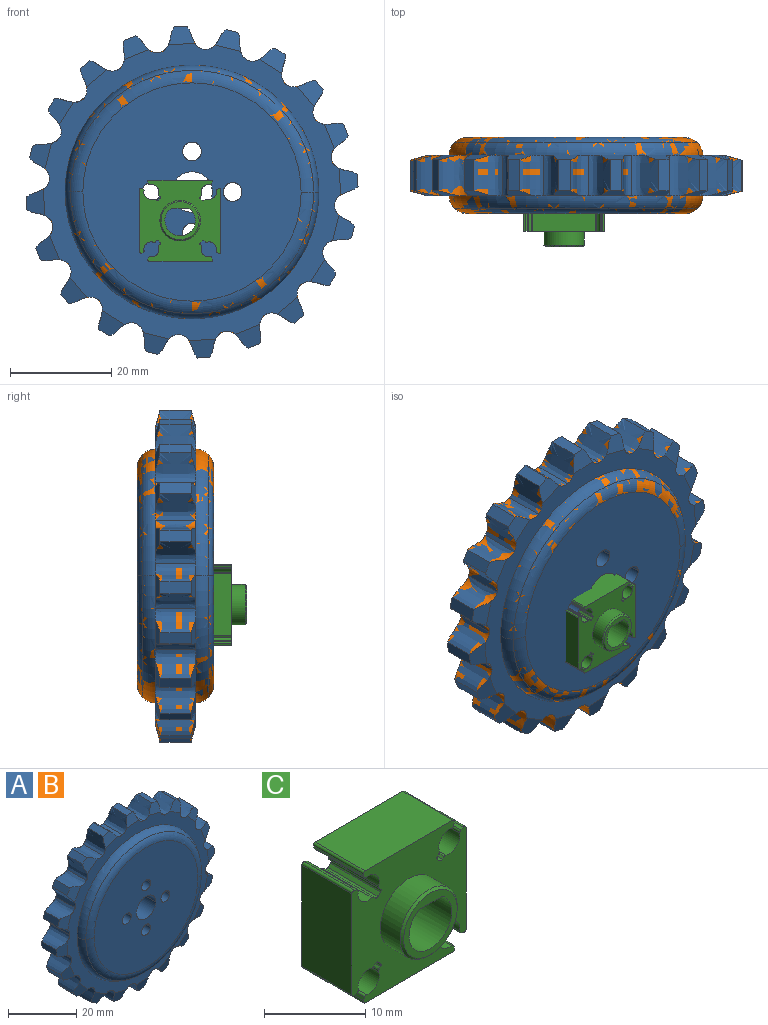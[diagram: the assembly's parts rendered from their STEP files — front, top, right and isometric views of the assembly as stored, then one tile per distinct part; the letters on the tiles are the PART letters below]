
ASSEMBLY  parts=3 mates=1
PART A: 134 faces, bbox 65.6x15.1x65.6 mm
  f0: plane 5.09x4.35mm, normal (-0.06,0.97,-0.25), area 14.3mm2, adj f1,f40,f43,f45
  f1: plane 6.12x2.3mm, normal (-0.24,0,-0.97), area 14.5mm2, adj f0,f43,f44,f45
  f2: plane 5.24x3.8mm, normal (0.02,0.97,-0.26), area 14.3mm2, adj f3,f40,f46,f48
  f3: plane 6.12x2.37mm, normal (0.07,0,-1), area 14.5mm2, adj f2,f46,f47,f48
  f4: plane 5.06x4.71mm, normal (0.1,0.97,-0.24), area 14.3mm2, adj f5,f40,f49,f51
  f5: plane 6.12x2.2mm, normal (0.37,0,-0.93), area 14.5mm2, adj f4,f49,f50,f51
  f6: plane 5.2x5.16mm, normal (0.17,0.97,-0.2), area 14.3mm2, adj f7,f40,f52,f54
  f7: plane 6.12x1.82mm, normal (0.64,0,-0.77), area 14.5mm2, adj f6,f52,f53,f54
  f8: plane 5.15x5.02mm, normal (0.22,0.97,-0.14), area 14.3mm2, adj f9,f40,f55,f57
  f9: plane 6.12x2.01mm, normal (0.85,0,-0.53), area 14.5mm2, adj f8,f55,f56,f57
  f10: plane 5.09x4.35mm, normal (0.25,0.97,-0.06), area 14.3mm2, adj f11,f40,f58,f60
  f11: plane 6.12x2.3mm, normal (0.97,0,-0.24), area 14.5mm2, adj f10,f58,f59,f60
  f12: plane 5.24x3.8mm, normal (0.26,0.97,0.02), area 14.3mm2, adj f13,f40,f61,f63
  f13: plane 6.12x2.37mm, normal (1,0,0.07), area 14.5mm2, adj f12,f61,f62,f63
  f14: plane 5.06x4.71mm, normal (0.24,0.97,0.1), area 14.3mm2, adj f15,f40,f64,f66
  f15: plane 6.12x2.2mm, normal (0.93,0,0.37), area 14.5mm2, adj f14,f64,f65,f66
  f16: plane 5.2x5.16mm, normal (0.2,0.97,0.17), area 14.3mm2, adj f17,f40,f67,f69
  f17: plane 6.12x1.82mm, normal (0.77,0,0.64), area 14.5mm2, adj f16,f67,f68,f69
  f18: plane 5.15x5.02mm, normal (0.14,0.97,0.22), area 14.3mm2, adj f19,f40,f70,f72
  f19: plane 6.12x2.01mm, normal (0.53,0,0.85), area 14.5mm2, adj f18,f70,f71,f72
  f20: plane 5.09x4.35mm, normal (0.06,0.97,0.25), area 14.3mm2, adj f21,f40,f73,f75
  f21: plane 6.12x2.3mm, normal (0.24,0,0.97), area 14.5mm2, adj f20,f73,f74,f75
  f22: plane 5.24x3.8mm, normal (-0.02,0.97,0.26), area 14.3mm2, adj f23,f40,f76,f78
  f23: plane 6.12x2.37mm, normal (-0.07,0,1), area 14.5mm2, adj f22,f76,f77,f78
  f24: plane 5.06x4.71mm, normal (-0.1,0.97,0.24), area 14.3mm2, adj f25,f40,f79,f81
  f25: plane 6.12x2.2mm, normal (-0.37,0,0.93), area 14.5mm2, adj f24,f79,f80,f81
  f26: plane 5.2x5.16mm, normal (-0.17,0.97,0.2), area 14.3mm2, adj f27,f40,f82,f84
  f27: plane 6.12x1.82mm, normal (-0.64,0,0.77), area 14.5mm2, adj f26,f82,f83,f84
  f28: plane 5.15x5.02mm, normal (-0.22,0.97,0.14), area 14.3mm2, adj f29,f40,f85,f87
  f29: plane 6.12x2.01mm, normal (-0.85,0,0.53), area 14.5mm2, adj f28,f85,f86,f87
  f30: plane 5.09x4.35mm, normal (-0.25,0.97,0.06), area 14.3mm2, adj f31,f40,f88,f90
  f31: plane 6.12x2.3mm, normal (-0.97,0,0.24), area 14.5mm2, adj f30,f88,f89,f90
  f32: plane 5.24x3.8mm, normal (-0.26,0.97,-0.02), area 14.3mm2, adj f33,f40,f91,f93
  f33: plane 6.12x2.37mm, normal (-1,0,-0.07), area 14.5mm2, adj f32,f91,f92,f93
  f34: plane 5.06x4.71mm, normal (-0.24,0.97,-0.1), area 14.3mm2, adj f35,f40,f94,f96
  f35: plane 6.12x2.2mm, normal (-0.93,0,-0.37), area 14.5mm2, adj f34,f94,f95,f96
  f36: plane 5.2x5.16mm, normal (-0.2,0.97,-0.17), area 14.3mm2, adj f37,f40,f97,f99
  f37: plane 6.12x1.82mm, normal (-0.77,0,-0.64), area 14.5mm2, adj f36,f97,f98,f99
  f38: plane 6.12x2.01mm, normal (-0.53,0,-0.85), area 14.5mm2, adj f39,f41,f42,f100
  f39: plane 5.15x5.02mm, normal (-0.14,0.97,-0.22), area 14.3mm2, adj f38,f40,f42,f100
  f40: plane 58.78x58.78mm, normal (0,1,0), area 667.1mm2, adj f0,f2,f4,f6,f8,f10,f12,f14
  f41: plane 5.15x5.02mm, normal (-0.14,-0.97,-0.22), area 14.3mm2, adj f38,f42,f100,f103
  f42: extruded ~8x5.32mm, area 45.7mm2, adj f38,f39,f40,f41,f43,f103
  f43: extruded ~8x5.51mm, area 45.8mm2, adj f0,f1,f40,f42,f44,f103
  f44: plane 5.09x4.35mm, normal (-0.06,-0.97,-0.25), area 14.3mm2, adj f1,f43,f45,f103
  f45: extruded ~8x4.31mm, area 45.7mm2, adj f0,f1,f40,f44,f46,f103
  f46: extruded ~8x4.64mm, area 45.8mm2, adj f2,f3,f40,f45,f47,f103
  f47: plane 5.24x3.8mm, normal (0.02,-0.97,-0.26), area 14.3mm2, adj f3,f46,f48,f103
  f48: extruded ~8x5.09mm, area 45.7mm2, adj f2,f3,f40,f47,f49,f103
  f49: extruded ~8x4.82mm, area 45.8mm2, adj f4,f5,f40,f48,f50,f103
  f50: plane 5.06x4.71mm, normal (0.1,-0.97,-0.24), area 14.3mm2, adj f5,f49,f51,f103
  f51: extruded ~8x5.73mm, area 45.7mm2, adj f4,f5,f40,f50,f52,f103
  f52: extruded ~8x5.6mm, area 45.8mm2, adj f6,f7,f40,f51,f53,f103
  f53: plane 5.2x5.16mm, normal (0.17,-0.97,-0.2), area 14.3mm2, adj f7,f52,f54,f103
  f54: extruded ~8x5.81mm, area 45.7mm2, adj f6,f7,f40,f53,f55,f103
  f55: extruded ~8x5.84mm, area 45.8mm2, adj f8,f9,f40,f54,f56,f103
  f56: plane 5.15x5.02mm, normal (0.22,-0.97,-0.14), area 14.3mm2, adj f9,f55,f57,f103
  f57: extruded ~8x5.32mm, area 45.7mm2, adj f8,f9,f40,f56,f58,f103
  f58: extruded ~8x5.51mm, area 45.8mm2, adj f10,f11,f40,f57,f59,f103
  f59: plane 5.09x4.35mm, normal (0.25,-0.97,-0.06), area 14.3mm2, adj f11,f58,f60,f103
  f60: extruded ~8x4.31mm, area 45.7mm2, adj f10,f11,f40,f59,f61,f103
  f61: extruded ~8x4.64mm, area 45.8mm2, adj f12,f13,f40,f60,f62,f103
  f62: plane 5.24x3.8mm, normal (0.26,-0.97,0.02), area 14.3mm2, adj f13,f61,f63,f103
  f63: extruded ~8x5.09mm, area 45.7mm2, adj f12,f13,f40,f62,f64,f103
  f64: extruded ~8x4.82mm, area 45.8mm2, adj f14,f15,f40,f63,f65,f103
  f65: plane 5.06x4.71mm, normal (0.24,-0.97,0.1), area 14.3mm2, adj f15,f64,f66,f103
  f66: extruded ~8x5.73mm, area 45.7mm2, adj f14,f15,f40,f65,f67,f103
  f67: extruded ~8x5.6mm, area 45.8mm2, adj f16,f17,f40,f66,f68,f103
  f68: plane 5.2x5.16mm, normal (0.2,-0.97,0.17), area 14.3mm2, adj f17,f67,f69,f103
  f69: extruded ~8x5.81mm, area 45.7mm2, adj f16,f17,f40,f68,f70,f103
  f70: extruded ~8x5.84mm, area 45.8mm2, adj f18,f19,f40,f69,f71,f103
  f71: plane 5.15x5.02mm, normal (0.14,-0.97,0.22), area 14.3mm2, adj f19,f70,f72,f103
  f72: extruded ~8x5.32mm, area 45.7mm2, adj f18,f19,f40,f71,f73,f103
  f73: extruded ~8x5.51mm, area 45.8mm2, adj f20,f21,f40,f72,f74,f103
  f74: plane 5.09x4.35mm, normal (0.06,-0.97,0.25), area 14.3mm2, adj f21,f73,f75,f103
  f75: extruded ~8x4.31mm, area 45.7mm2, adj f20,f21,f40,f74,f76,f103
  f76: extruded ~8x4.64mm, area 45.8mm2, adj f22,f23,f40,f75,f77,f103
  f77: plane 5.24x3.8mm, normal (-0.02,-0.97,0.26), area 14.3mm2, adj f23,f76,f78,f103
  f78: extruded ~8x5.09mm, area 45.7mm2, adj f22,f23,f40,f77,f79,f103
  f79: extruded ~8x4.82mm, area 45.8mm2, adj f24,f25,f40,f78,f80,f103
  f80: plane 5.06x4.71mm, normal (-0.1,-0.97,0.24), area 14.3mm2, adj f25,f79,f81,f103
  f81: extruded ~8x5.73mm, area 45.7mm2, adj f24,f25,f40,f80,f82,f103
  f82: extruded ~8x5.6mm, area 45.8mm2, adj f26,f27,f40,f81,f83,f103
  f83: plane 5.2x5.16mm, normal (-0.17,-0.97,0.2), area 14.3mm2, adj f27,f82,f84,f103
  f84: extruded ~8x5.81mm, area 45.8mm2, adj f26,f27,f40,f83,f85,f103
  f85: extruded ~8x5.84mm, area 45.7mm2, adj f28,f29,f40,f84,f86,f103
  f86: plane 5.15x5.02mm, normal (-0.22,-0.97,0.14), area 14.3mm2, adj f29,f85,f87,f103
  f87: extruded ~8x5.32mm, area 45.7mm2, adj f28,f29,f40,f86,f88,f103
  f88: extruded ~8x5.51mm, area 45.8mm2, adj f30,f31,f40,f87,f89,f103
  f89: plane 5.09x4.35mm, normal (-0.25,-0.97,0.06), area 14.3mm2, adj f31,f88,f90,f103
  f90: extruded ~8x4.31mm, area 45.7mm2, adj f30,f31,f40,f89,f91,f103
  f91: extruded ~8x4.64mm, area 45.8mm2, adj f32,f33,f40,f90,f92,f103
  f92: plane 5.24x3.8mm, normal (-0.26,-0.97,-0.02), area 14.3mm2, adj f33,f91,f93,f103
  f93: extruded ~8x5.09mm, area 45.7mm2, adj f32,f33,f40,f92,f94,f103
  f94: extruded ~8x4.82mm, area 45.8mm2, adj f34,f35,f40,f93,f95,f103
  f95: plane 5.06x4.71mm, normal (-0.24,-0.97,-0.1), area 14.3mm2, adj f35,f94,f96,f103
  f96: extruded ~8x5.73mm, area 45.7mm2, adj f34,f35,f40,f95,f97,f103
  f97: extruded ~8x5.6mm, area 45.8mm2, adj f36,f37,f40,f96,f98,f103
  f98: plane 5.2x5.16mm, normal (-0.2,-0.97,-0.17), area 14.3mm2, adj f37,f97,f99,f103
  f99: extruded ~8x5.81mm, area 45.7mm2, adj f36,f37,f40,f98,f100,f103
  f100: extruded ~8x5.84mm, area 45.8mm2, adj f38,f39,f40,f41,f99,f103
  f101: torus R=21.5mm, axis (0,1,0), area 212.9mm2, adj f40,f102,f104
  f102: torus R=21.5mm, axis (0,1,0), area 212.9mm2, adj f40,f101,f105
  f103: plane 58.78x58.78mm, normal (0,-1,0), area 667.1mm2, adj f41,f42,f43,f44,f45,f46,f47,f48
  f104: torus R=21.5mm, axis (0,1,0), area 196.9mm2, adj f101,f105,f117
  f105: torus R=21.5mm, axis (0,1,0), area 196.9mm2, adj f102,f104,f117
  f106: cylinder r=3mm len=7.5mm, axis (0,1,0), area 70.7mm2, adj f107,f115,f117
  f107: cylinder r=3mm len=7.5mm, axis (0,1,0), area 70.7mm2, adj f106,f115,f117
  f108: cylinder r=3mm len=7.5mm, axis (0,1,0), area 70.7mm2, adj f109,f114,f117
  f109: cylinder r=3mm len=7.5mm, axis (0,1,0), area 70.7mm2, adj f108,f114,f117
  f110: cylinder r=3mm len=7.5mm, axis (0,1,0), area 70.7mm2, adj f111,f116,f117
  f111: cylinder r=3mm len=7.5mm, axis (0,1,0), area 70.7mm2, adj f110,f116,f117
  f112: torus R=21.5mm, axis (0,-1,0), area 212.9mm2, adj f103,f113,f118
  f113: torus R=21.5mm, axis (0,-1,0), area 212.9mm2, adj f103,f112,f119
  f114: plane 6.02x6mm, normal (0,1,0), area 17.5mm2, adj f108,f109,f120,f121
  f115: plane 6.02x6mm, normal (0,1,0), area 17.5mm2, adj f106,f107,f122,f123
  f116: plane 6.02x6mm, normal (0,1,0), area 17.5mm2, adj f110,f111,f124,f125
  f117: plane 43.04x43mm, normal (0,1,0), area 1288.8mm2, adj f104,f105,f106,f107,f108,f109,f110,f111
  f118: torus R=21.5mm, axis (0,-1,0), area 196.9mm2, adj f112,f119,f130
  f119: torus R=21.5mm, axis (0,-1,0), area 196.9mm2, adj f113,f118,f130
  f120: cylinder r=1.85mm len=7.5mm, axis (0,1,0), area 43.6mm2, adj f114,f121,f130
  f121: cylinder r=1.85mm len=7.5mm, axis (0,1,0), area 43.6mm2, adj f114,f120,f130
  f122: cylinder r=1.85mm len=7.5mm, axis (0,1,0), area 43.6mm2, adj f115,f123,f130
  f123: cylinder r=1.85mm len=7.5mm, axis (0,1,0), area 43.6mm2, adj f115,f122,f130
  f124: cylinder r=1.85mm len=7.5mm, axis (0,1,0), area 43.6mm2, adj f116,f125,f130
  f125: cylinder r=1.85mm len=7.5mm, axis (0,1,0), area 43.6mm2, adj f116,f124,f130
  f126: cylinder r=4mm len=15mm, axis (0,1,0), area 188.5mm2, adj f117,f127,f130
  f127: cylinder r=4mm len=15mm, axis (0,1,0), area 188.5mm2, adj f117,f126,f130
  f128: cylinder r=3mm len=7.5mm, axis (0,1,0), area 70.7mm2, adj f117,f129,f131
  f129: cylinder r=3mm len=7.5mm, axis (0,1,0), area 70.7mm2, adj f117,f128,f131
  f130: plane 43.04x43mm, normal (0,-1,0), area 1358.9mm2, adj f118,f119,f120,f121,f122,f123,f124,f125
  f131: plane 6.02x6mm, normal (0,1,0), area 17.5mm2, adj f128,f129,f132,f133
  f132: cylinder r=1.85mm len=7.5mm, axis (0,1,0), area 43.6mm2, adj f130,f131,f133
  f133: cylinder r=1.85mm len=7.5mm, axis (0,1,0), area 43.6mm2, adj f130,f131,f132
PART B: same geometry as A
PART C: 72 faces, bbox 16x10x16 mm
  f0: cone r=3.75mm half-angle=45deg, axis (0,1,0), area 8.7mm2, adj f2,f71
  f1: cylinder r=2.02mm len=5mm, axis (0,0,-1), area 63.4mm2, adj f3,f46
  f2: cylinder r=4mm len=8mm, axis (0,1,0), area 68.9mm2, adj f0,f16
  f3: cylinder r=3mm len=10mm, axis (0,1,0), area 139.5mm2, adj f1,f69,f70,f71
  f4: cylinder r=1.49mm len=7mm, axis (0,1,0), area 21.9mm2, adj f16,f17,f68,f70
  f5: cylinder r=0.25mm len=7mm, axis (0,1,0), area 2.8mm2, adj f16,f66,f67,f70
  f6: cylinder r=0.25mm len=7mm, axis (0,1,0), area 2.5mm2, adj f16,f61,f62,f70
  f7: cylinder r=0.25mm len=7mm, axis (0,1,0), area 2.5mm2, adj f16,f56,f57,f70
  f8: cylinder r=0.25mm len=7mm, axis (0,1,0), area 2.8mm2, adj f16,f51,f52,f70
  f9: cylinder r=1.49mm len=7mm, axis (0,1,0), area 21.9mm2, adj f16,f49,f50,f70
  f10: cylinder r=0.25mm len=7mm, axis (0,1,0), area 3.4mm2, adj f16,f45,f46,f70
  f11: cylinder r=0.25mm len=7mm, axis (0,1,0), area 2mm2, adj f16,f42,f43,f70
  f12: cylinder r=1.49mm len=7mm, axis (0,1,0), area 21.9mm2, adj f16,f36,f37,f70
  f13: cylinder r=1.49mm len=7mm, axis (0,1,0), area 21.9mm2, adj f16,f29,f30,f70
  f14: cylinder r=0.25mm len=7mm, axis (0,1,0), area 2mm2, adj f16,f23,f24,f70
  f15: cylinder r=0.25mm len=7mm, axis (0,1,0), area 3.4mm2, adj f16,f20,f21,f70
  f16: plane 16x16mm, normal (0,-1,0), area 164.9mm2, adj f2,f4,f5,f6,f7,f8,f9,f10
  f17: cylinder r=0.25mm len=7mm, axis (0,1,0), area 2.5mm2, adj f4,f16,f18,f70
  f18: plane 7x0.39mm, normal (0.94,0,-0.34), area 2.9mm2, adj f16,f17,f19,f70
  f19: cylinder r=0.25mm len=7mm, axis (0,1,0), area 3.4mm2, adj f16,f18,f20,f70
  f20: plane 12.29x7mm, normal (0,0,1), area 86.1mm2, adj f15,f16,f19,f70
  f21: plane 7x0.39mm, normal (-0.94,0,-0.34), area 2.9mm2, adj f15,f16,f22,f70
  f22: cylinder r=0.25mm len=7mm, axis (0,1,0), area 2.5mm2, adj f16,f21,f23,f70
  f23: cylinder r=1.49mm len=7mm, axis (0,1,0), area 21.9mm2, adj f14,f16,f22,f70
  f24: plane 7x0.21mm, normal (-0.71,0,-0.71), area 2.1mm2, adj f14,f16,f25,f70
  f25: cylinder r=0.25mm len=7mm, axis (0,1,0), area 2.8mm2, adj f16,f24,f26,f70
  f26: plane 7x0.36mm, normal (-0.71,0,0.71), area 3.6mm2, adj f16,f25,f27,f70
  f27: cylinder r=0.25mm len=7mm, axis (0,1,0), area 2.8mm2, adj f16,f26,f28,f70
  f28: plane 7x0.21mm, normal (0.71,0,0.71), area 2.1mm2, adj f16,f27,f29,f70
  f29: cylinder r=0.25mm len=7mm, axis (0,1,0), area 2mm2, adj f13,f16,f28,f70
  f30: cylinder r=0.25mm len=7mm, axis (0,1,0), area 2.5mm2, adj f13,f16,f31,f70
  f31: plane 7x0.39mm, normal (0.34,0,0.94), area 2.9mm2, adj f16,f30,f32,f70
  f32: cylinder r=0.25mm len=7mm, axis (0,1,0), area 3.4mm2, adj f16,f31,f33,f70
  f33: plane 12.29x7mm, normal (-1,0,0), area 86.1mm2, adj f16,f32,f34,f70
  f34: cylinder r=0.25mm len=7mm, axis (0,1,0), area 3.4mm2, adj f16,f33,f35,f70
  f35: plane 7x0.39mm, normal (0.34,0,-0.94), area 2.9mm2, adj f16,f34,f36,f70
  f36: cylinder r=0.25mm len=7mm, axis (0,1,0), area 2.5mm2, adj f12,f16,f35,f70
  f37: cylinder r=0.25mm len=7mm, axis (0,1,0), area 2mm2, adj f12,f16,f38,f70
  f38: plane 7x0.21mm, normal (0.71,0,-0.71), area 2.1mm2, adj f16,f37,f39,f70
  f39: cylinder r=0.25mm len=7mm, axis (0,1,0), area 2.8mm2, adj f16,f38,f40,f70
  f40: plane 7x0.36mm, normal (-0.71,0,-0.71), area 3.6mm2, adj f16,f39,f41,f70
  f41: cylinder r=0.25mm len=7mm, axis (0,1,0), area 2.8mm2, adj f16,f40,f42,f70
  f42: plane 7x0.21mm, normal (-0.71,0,0.71), area 2.1mm2, adj f11,f16,f41,f70
  f43: cylinder r=1.49mm len=7mm, axis (0,1,0), area 21.9mm2, adj f11,f16,f44,f70
  f44: cylinder r=0.25mm len=7mm, axis (0,1,0), area 2.5mm2, adj f16,f43,f45,f70
  f45: plane 7x0.39mm, normal (-0.94,0,0.34), area 2.9mm2, adj f10,f16,f44,f70
  f46: plane 12.29x7mm, normal (0,0,-1), area 73.2mm2, adj f1,f10,f16,f47,f70
  f47: cylinder r=0.25mm len=7mm, axis (0,1,0), area 3.4mm2, adj f16,f46,f48,f70
  f48: plane 7x0.39mm, normal (0.94,0,0.34), area 2.9mm2, adj f16,f47,f49,f70
  f49: cylinder r=0.25mm len=7mm, axis (0,1,0), area 2.5mm2, adj f9,f16,f48,f70
  f50: cylinder r=0.25mm len=7mm, axis (0,1,0), area 2mm2, adj f9,f16,f51,f70
  f51: plane 7x0.21mm, normal (0.71,0,0.71), area 2.1mm2, adj f8,f16,f50,f70
  f52: plane 7x0.36mm, normal (0.71,0,-0.71), area 3.6mm2, adj f8,f16,f53,f70
  f53: cylinder r=0.25mm len=7mm, axis (0,1,0), area 2.8mm2, adj f16,f52,f54,f70
  f54: plane 7x0.21mm, normal (-0.71,0,-0.71), area 2.1mm2, adj f16,f53,f55,f70
  f55: cylinder r=0.25mm len=7mm, axis (0,1,0), area 2mm2, adj f16,f54,f56,f70
  f56: cylinder r=1.49mm len=7mm, axis (0,1,0), area 21.9mm2, adj f7,f16,f55,f70
  f57: plane 7x0.39mm, normal (-0.34,0,-0.94), area 2.9mm2, adj f7,f16,f58,f70
  f58: cylinder r=0.25mm len=7mm, axis (0,1,0), area 3.4mm2, adj f16,f57,f59,f70
  f59: plane 12.29x7mm, normal (1,0,0), area 86.1mm2, adj f16,f58,f60,f70
  f60: cylinder r=0.25mm len=7mm, axis (0,1,0), area 3.4mm2, adj f16,f59,f61,f70
  f61: plane 7x0.39mm, normal (-0.34,0,0.94), area 2.9mm2, adj f6,f16,f60,f70
  f62: cylinder r=1.49mm len=7mm, axis (0,1,0), area 21.9mm2, adj f6,f16,f63,f70
  f63: cylinder r=0.25mm len=7mm, axis (0,1,0), area 2mm2, adj f16,f62,f64,f70
  f64: plane 7x0.21mm, normal (-0.71,0,0.71), area 2.1mm2, adj f16,f63,f65,f70
  f65: cylinder r=0.25mm len=7mm, axis (0,1,0), area 2.8mm2, adj f16,f64,f66,f70
  f66: plane 7x0.36mm, normal (0.71,0,0.71), area 3.6mm2, adj f5,f16,f65,f70
  f67: plane 7x0.21mm, normal (0.71,0,-0.71), area 2.1mm2, adj f5,f16,f68,f70
  f68: cylinder r=0.25mm len=7mm, axis (0,1,0), area 2mm2, adj f4,f16,f67,f70
  f69: plane 10x3.32mm, normal (0,0,-1), area 33.2mm2, adj f3,f70,f71
  f70: plane 16x16mm, normal (0,1,0), area 188mm2, adj f3,f4,f5,f6,f7,f8,f9,f10
  f71: plane 7.49x7.49mm, normal (0,-1,0), area 16.9mm2, adj f0,f3,f69
PLACE A at identity
PLACE B at identity
PLACE C t=(17.68,7.51,1.62)mm
MATE cylindrical C.f13 <-> A.f128  axis (0,1,0) through (-8,-11.5,0)mm
